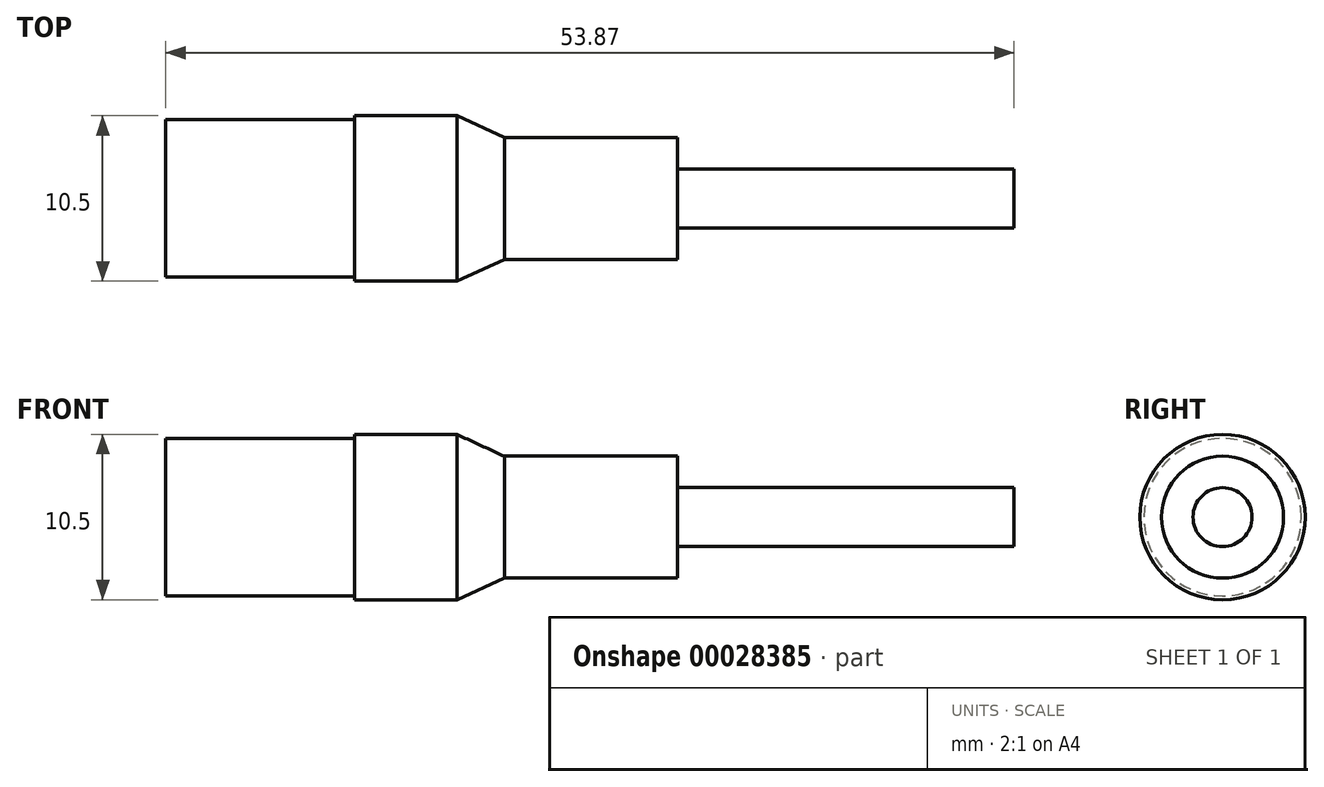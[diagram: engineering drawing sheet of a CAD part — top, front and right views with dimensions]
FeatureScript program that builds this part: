
annotation { "Feature Type Name" : "Feature", "Feature Type Description" : "" }
export const myFeature = defineFeature(function(context is Context, id is Id, definition is map)
    precondition{}
    {
        {
            var Q0;
            Q0=qCreatedBy(makeId("Front.planeOp"),FACE);
            var sketch = newSketch(context, id + "F0", { "sketchPlane" : qUnion([Q0])});
            skLineSegment(sketch, "E0.rect.bottom", {"start": v(-6, 5) * mm, "end": v(6, 5) * mm});
            skLineSegment(sketch, "E0.rect.top", {"start": v(-6, -5) * mm, "end": v(6, -5) * mm, "construction": true});
            skLineSegment(sketch, "E0.rect.left", {"start": v(-6, 5) * mm, "end": v(-6, 0) * mm});
            skLineSegment(sketch, "E0.rect.right", {"start": v(6, 5) * mm, "end": v(6, -5) * mm, "construction": true});
            skPoint(sketch, "E0.rect.middle", {"position": v(0, 0) * mm});
            skLineSegment(sketch, "E1.rect.bottom", {"start": v(6, 5.25) * mm, "end": v(12.5, 5.25) * mm});
            skLineSegment(sketch, "E1.rect.top", {"start": v(6, -5.25) * mm, "end": v(12.5, -5.25) * mm, "construction": true});
            skLineSegment(sketch, "E1.rect.left", {"start": v(6, 5.25) * mm, "end": v(6, 5) * mm});
            skLineSegment(sketch, "E1.rect.right", {"start": v(12.5, 5.25) * mm, "end": v(12.5, -5.25) * mm});
            skPoint(sketch, "E1.rect.middle", {"position": v(9.25, 0) * mm});
            skLineSegment(sketch, "E2.rect.bottom", {"start": v(12.5, 5.25) * mm, "end": v(15.5, 3.88) * mm});
            skLineSegment(sketch, "E2.rect.top", {"start": v(12.5, -5.25) * mm, "end": v(15.5, -3.87) * mm, "construction": true});
            skLineSegment(sketch, "E2.rect.right", {"start": v(15.5, 3.88) * mm, "end": v(15.5, -3.87) * mm, "construction": true});
            skPoint(sketch, "E2.rect.middle", {"position": v(14, 0) * mm});
            skLineSegment(sketch, "E3.rect.bottom", {"start": v(15.5, 3.88) * mm, "end": v(26.5, 3.88) * mm});
            skLineSegment(sketch, "E3.rect.top", {"start": v(15.5, -3.87) * mm, "end": v(26.5, -3.87) * mm, "construction": true});
            skLineSegment(sketch, "E3.rect.right", {"start": v(26.5, 3.88) * mm, "end": v(26.5, 1.87) * mm});
            skPoint(sketch, "E3.rect.middle", {"position": v(21, 0) * mm});
            skLineSegment(sketch, "E4.rect.bottom", {"start": v(26.5, 1.87) * mm, "end": v(47.87, 1.87) * mm});
            skLineSegment(sketch, "E4.rect.top", {"start": v(26.5, -1.88) * mm, "end": v(47.87, -1.87) * mm, "construction": true});
            skLineSegment(sketch, "E4.rect.left", {"start": v(26.5, 1.87) * mm, "end": v(26.5, -1.88) * mm, "construction": true});
            skLineSegment(sketch, "E4.rect.right", {"start": v(47.87, 1.87) * mm, "end": v(47.87, 0) * mm});
            skPoint(sketch, "E4.rect.middle", {"position": v(37.18, 0) * mm});
            skLineSegment(sketch, "E5", {"start": v(-6, 0) * mm, "end": v(47.87, 0) * mm});
            skLineSegment(sketch, "E6", {"start": v(47.87, 0) * mm, "end": v(47.87, -1.87) * mm, "construction": true});
            skLineSegment(sketch, "E7", {"start": v(26.5, 1.87) * mm, "end": v(26.5, -3.87) * mm, "construction": true});
            skLineSegment(sketch, "E8", {"start": v(6, 5) * mm, "end": v(6, -5.25) * mm, "construction": true});
            skLineSegment(sketch, "E9", {"start": v(-6, 0) * mm, "end": v(-6, -5) * mm, "construction": true});
            skSolve(sketch);
        }
        {
            var Q0;
            Q0 = qSketchRegion(id + "F0", true);
            var Q1;
            Q1=sQuery(id+"F0.wireOp",EDGE,"E5");
            revolve(context, id + "F1", {"entities" : qUnion([Q0]), "axis" : qUnion([Q1]), "revolveType" : RevolveType.FULL});
        }
    });
